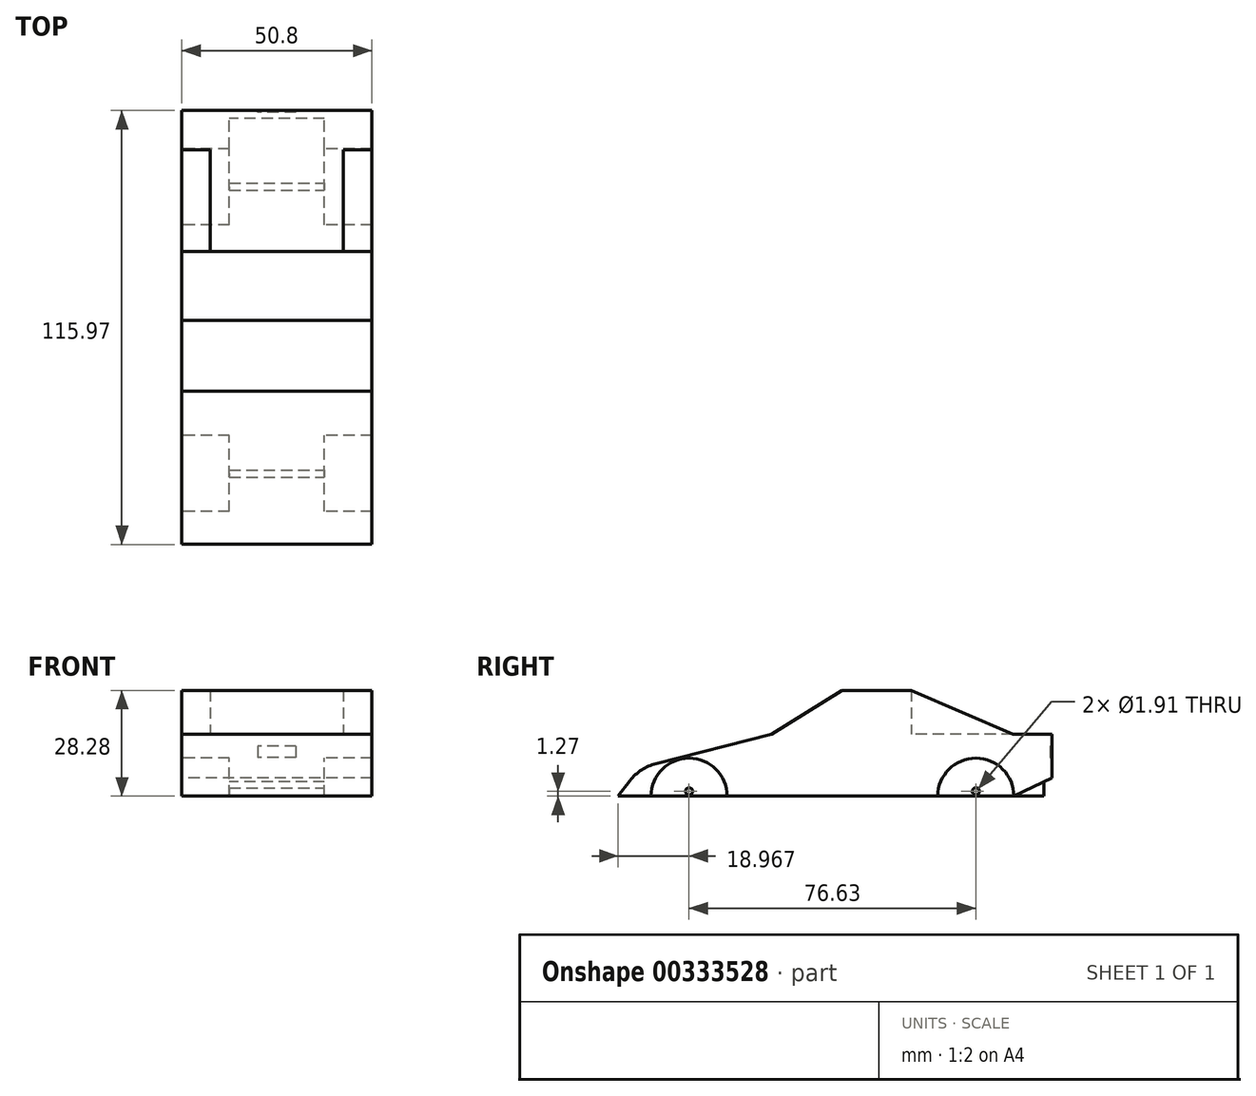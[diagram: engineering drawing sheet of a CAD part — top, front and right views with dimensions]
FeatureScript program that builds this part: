
annotation { "Feature Type Name" : "Feature", "Feature Type Description" : "" }
export const myFeature = defineFeature(function(context is Context, id is Id, definition is map)
    precondition{}
    {
        {
            var Q0;
            Q0=qCreatedBy(makeId("Right.planeOp"),FACE);
            var sketch = newSketch(context, id + "F0", { "sketchPlane" : qUnion([Q0])});
            skLineSegment(sketch, "E0", {"start": v(0, 0) * mm, "end": v(-35.1, -8.9) * mm});
            skLineSegment(sketch, "E1", {"start": v(-35.1, -8.9) * mm, "end": v(-40.98, -16.51) * mm});
            skLineSegment(sketch, "E2", {"start": v(-40.98, -16.51) * mm, "end": v(-32.17, -16.51) * mm});
            skArc(sketch, "E3", {"start": v(-32.17, -16.51) * mm, "mid": v(-22.01, -6.35) * mm, "end": v(-11.85, -16.51) * mm});
            skLineSegment(sketch, "E4", {"start": v(0, 0) * mm, "end": v(18.87, 11.77) * mm});
            skLineSegment(sketch, "E5", {"start": v(18.87, 11.77) * mm, "end": v(37.3, 11.77) * mm});
            skLineSegment(sketch, "E6", {"start": v(37.3, 11.77) * mm, "end": v(64.55, 0) * mm});
            skLineSegment(sketch, "E7", {"start": v(64.55, 0) * mm, "end": v(75, 0) * mm});
            skLineSegment(sketch, "E8", {"start": v(75, 0) * mm, "end": v(75, -11.69) * mm});
            skLineSegment(sketch, "E9", {"start": v(75, -11.69) * mm, "end": v(64.78, -16.51) * mm});
            skPoint(sketch, "E10.center.orphan", {"position": v(48.94, -16.51) * mm});
            skPoint(sketch, "E10.end.orphan", {"position": v(37.99, -16.51) * mm});
            skPoint(sketch, "E11.end.orphan", {"position": v(59.1, -16.51) * mm});
            skArc(sketch, "E12", {"start": v(64.78, -16.51) * mm, "mid": v(54.62, -6.35) * mm, "end": v(44.46, -16.51) * mm});
            skLineSegment(sketch, "E13", {"start": v(-11.85, -16.51) * mm, "end": v(44.46, -16.51) * mm});
            skSolve(sketch);
        }
        {
            var Q0;
            Q0 = qSketchRegion(id + "F0", true);
            extrude(context, id + "F1", {"entities" : qUnion([Q0]), "depth" : 50.8 * mm, "offsetDistance" : 25.4 * mm, "symmetric" : true});
        }
        {
            var Q0;
            Q0=makeQuery(id+"F1.opExtrude","SWEPT_FACE",FACE,{"disambiguationData":[OSD([sQuery(id+"F0.wireOp",EDGE,"E7")])]});
            var sketch = newSketch(context, id + "F2", { "sketchPlane" : qUnion([Q0])});
            skLineSegment(sketch, "E14.left", {"start": v(-17.78, 64.55) * mm, "end": v(-17.78, 37.3) * mm});
            skLineSegment(sketch, "E15.MirrorCS", {"start": v(17.78, 64.55) * mm, "end": v(17.78, 37.3) * mm});
            skPoint(sketch, "E14.top.end.orphan", {"position": v(0, 37.3) * mm});
            skLineSegment(sketch, "E16", {"start": v(-17.78, 37.3) * mm, "end": v(17.78, 37.3) * mm});
            skLineSegment(sketch, "E17", {"start": v(-17.78, 64.55) * mm, "end": v(17.78, 64.55) * mm});
            skSolve(sketch);
        }
        {
            var Q0;
            Q0 = qSketchRegion(id + "F2", true);
            extrude(context, id + "F3", {"entities" : qUnion([Q0]), "operationType" : NewBodyOperationType.REMOVE, "endBound" : BoundingType.THROUGH_ALL, "depth" : 25.4 * mm, "offsetDistance" : 25.4 * mm});
        }
        {
            var Q0;
            Q0=makeQuery(id+"F1.opExtrude","SWEPT_FACE",FACE,{"disambiguationData":[OSD([sQuery(id+"F0.wireOp",EDGE,"E13")])]});
            var sketch = newSketch(context, id + "F4", { "sketchPlane" : qUnion([Q0])});
            skLineSegment(sketch, "E18.top", {"start": v(0, -72.81) * mm, "end": v(-12.7, -72.81) * mm});
            skLineSegment(sketch, "E18.right", {"start": v(-12.7, 32.17) * mm, "end": v(-12.7, -72.81) * mm});
            skLineSegment(sketch, "E19.MirrorCS", {"start": v(12.7, 32.17) * mm, "end": v(12.7, -72.81) * mm});
            skLineSegment(sketch, "E20.MirrorCS", {"start": v(0, -72.81) * mm, "end": v(12.7, -72.81) * mm});
            skPoint(sketch, "E18.bottom.start.orphan", {"position": v(0, 36.4) * mm});
            skPoint(sketch, "E21.MirrorCS.end.orphan", {"position": v(12.7, 36.4) * mm});
            skLineSegment(sketch, "E22", {"start": v(-12.7, 32.17) * mm, "end": v(12.7, 32.17) * mm});
            skPoint(sketch, "E23.orphan", {"position": v(-12.7, 36.4) * mm});
            skSolve(sketch);
        }
        {
            var Q0;
            Q0 = qSketchRegion(id + "F4", true);
            extrude(context, id + "F5", {"entities" : qUnion([Q0]), "operationType" : NewBodyOperationType.ADD, "oppositeDirection" : true, "depth" : 10.16 * mm, "offsetDistance" : 25.4 * mm});
        }
        {
            var Q0;
            Q0=makeQuery(id+"F1.opExtrude","SWEPT_FACE",FACE,{"disambiguationData":[OSD([sQuery(id+"F0.wireOp",EDGE,"E0")])]});
            var sketch = newSketch(context, id + "F6", { "sketchPlane" : qUnion([Q0])});
            skLineSegment(sketch, "E24.bottom", {"start": v(-25.4, -36.22) * mm, "end": v(25.4, -36.22) * mm});
            skLineSegment(sketch, "E24.top", {"start": v(-25.4, 0) * mm, "end": v(25.4, 0) * mm});
            skLineSegment(sketch, "E24.left", {"start": v(-25.4, -36.22) * mm, "end": v(-25.4, 0) * mm});
            skLineSegment(sketch, "E24.right", {"start": v(25.4, -36.22) * mm, "end": v(25.4, 0) * mm});
            skSolve(sketch);
        }
        {
            var Q0;
            Q0 = qSketchRegion(id + "F6", true);
            extrude(context, id + "F7", {"entities" : qUnion([Q0]), "operationType" : NewBodyOperationType.REMOVE, "endBound" : BoundingType.THROUGH_ALL, "depth" : 25.4 * mm, "offsetDistance" : 25.4 * mm});
        }
        {
            var Q0;
            Q0=makeQuery(id+"F1.opExtrude","SWEPT_EDGE",EDGE,{"disambiguationData":[OSD([sQuery(id+"F0.wireOp",EDGE,"E0"),sQuery(id+"F0.wireOp",EDGE,"E1")])]});
            fillet(context, id + "F8", {"entities" : qUnion([Q0]), "radius" : 12.7 * mm, "tangentPropagation" : true, "allowEdgeOverflow" : false});
        }
        {
            var Q0;
            Q0=makeQuery(id+"F1.opExtrude","SWEPT_FACE",FACE,{"disambiguationData":[OSD([sQuery(id+"F0.wireOp",EDGE,"E8")])]});
            var sketch = newSketch(context, id + "F9", { "sketchPlane" : qUnion([Q0])});
            skLineSegment(sketch, "E25.bottom", {"start": v(-5.08, -3.16) * mm, "end": v(5.08, -3.16) * mm});
            skLineSegment(sketch, "E25.top", {"start": v(-5.08, -6.2) * mm, "end": v(5.08, -6.2) * mm});
            skLineSegment(sketch, "E25.left", {"start": v(-5.08, -3.16) * mm, "end": v(-5.08, -6.2) * mm});
            skLineSegment(sketch, "E25.right", {"start": v(5.08, -3.16) * mm, "end": v(5.08, -6.2) * mm});
            skPoint(sketch, "E25.middle", {"position": v(0, -4.69) * mm});
            skSolve(sketch);
        }
        {
            var Q0;
            Q0 = qSketchRegion(id + "F9", true);
            extrude(context, id + "F10", {"entities" : qUnion([Q0]), "operationType" : NewBodyOperationType.REMOVE, "oppositeDirection" : true, "depth" : 0.5 * mm, "offsetDistance" : 25.4 * mm});
        }
        {
            var Q0;
            {var subQ0=sQuery(id+"F4.wireOp",EDGE,"E19.MirrorCS");Q0=makeQuery(id+"F5.boolean.opBoolean","SPLIT",FACE,{"disambiguationData":[TD([makeQuery(id+"F1.opExtrude","SWEPT_FACE",FACE,{"disambiguationData":[OSD([sQuery(id+"F0.wireOp",EDGE,"E2")])]}),makeQuery(id+"F1.opExtrude","SWEPT_FACE",FACE,{"disambiguationData":[OSD([sQuery(id+"F0.wireOp",EDGE,"E3")])]}),makeQuery(id+"F1.opExtrude","SWEPT_FACE",FACE,{"disambiguationData":[OSD([sQuery(id+"F0.wireOp",EDGE,"E13")])]}),makeQuery(id+"F5.opExtrude","CAP_FACE",FACE,{"disambiguationData":[OSD([sQuery(id+"F4.wireOp",EDGE,"E18.top"),sQuery(id+"F4.wireOp",EDGE,"E18.right"),subQ0,sQuery(id+"F4.wireOp",EDGE,"E20.MirrorCS"),sQuery(id+"F4.wireOp",EDGE,"E22")])],"isStart":true})])],"derivedFrom":makeQuery(id+"F5.opExtrude","SWEPT_FACE",FACE,{"disambiguationData":[OSD([subQ0])]})});}
            var sketch = newSketch(context, id + "F11", { "sketchPlane" : qUnion([Q0])});
            skCircle(sketch, "E26", {"center": v(-22.01, -15.24) * mm, "radius": 0.95 * mm});
            skPoint(sketch, "E26.centerSnap0", {"position": v(-22.01, -16.51) * mm});
            skSolve(sketch);
        }
        {
            var Q0;
            Q0 = qSketchRegion(id + "F11", true);
            extrude(context, id + "F12", {"entities" : qUnion([Q0]), "operationType" : NewBodyOperationType.REMOVE, "endBound" : BoundingType.THROUGH_ALL, "oppositeDirection" : true, "depth" : 25.4 * mm, "offsetDistance" : 25.4 * mm});
        }
        {
            var Q0;
            {var subQ0=sQuery(id+"F4.wireOp",EDGE,"E19.MirrorCS");var subQ1=makeQuery(id+"F5.opExtrude","SWEPT_FACE",FACE,{"disambiguationData":[OSD([subQ0])]});Q0=makeQuery(id+"F5.boolean.opBoolean","SPLIT",FACE,{"disambiguationData":[TD([makeQuery(id+"F1.opExtrude","SWEPT_FACE",FACE,{"disambiguationData":[OSD([sQuery(id+"F0.wireOp",EDGE,"E2")])]}),makeQuery(id+"F1.opExtrude","SWEPT_FACE",FACE,{"disambiguationData":[OSD([sQuery(id+"F0.wireOp",EDGE,"E9")])]}),makeQuery(id+"F1.opExtrude","SWEPT_FACE",FACE,{"disambiguationData":[OSD([sQuery(id+"F0.wireOp",EDGE,"E12")])]}),makeQuery(id+"F1.opExtrude","SWEPT_FACE",FACE,{"disambiguationData":[OSD([sQuery(id+"F0.wireOp",EDGE,"E13")])]}),makeQuery(id+"F5.opExtrude","CAP_FACE",FACE,{"disambiguationData":[OSD([sQuery(id+"F4.wireOp",EDGE,"E18.top"),sQuery(id+"F4.wireOp",EDGE,"E18.right"),subQ0,sQuery(id+"F4.wireOp",EDGE,"E20.MirrorCS"),sQuery(id+"F4.wireOp",EDGE,"E22")])],"isStart":true}),subQ1])],"derivedFrom":subQ1});}
            var sketch = newSketch(context, id + "F13", { "sketchPlane" : qUnion([Q0])});
            skCircle(sketch, "E27", {"center": v(54.62, -15.24) * mm, "radius": 0.95 * mm});
            skPoint(sketch, "E27.centerSnap0", {"position": v(54.62, -16.51) * mm});
            skSolve(sketch);
        }
        {
            var Q0;
            Q0 = qSketchRegion(id + "F13", true);
            extrude(context, id + "F14", {"entities" : qUnion([Q0]), "operationType" : NewBodyOperationType.REMOVE, "endBound" : BoundingType.THROUGH_ALL, "oppositeDirection" : true, "depth" : 25.4 * mm, "offsetDistance" : 25.4 * mm});
        }
    });
